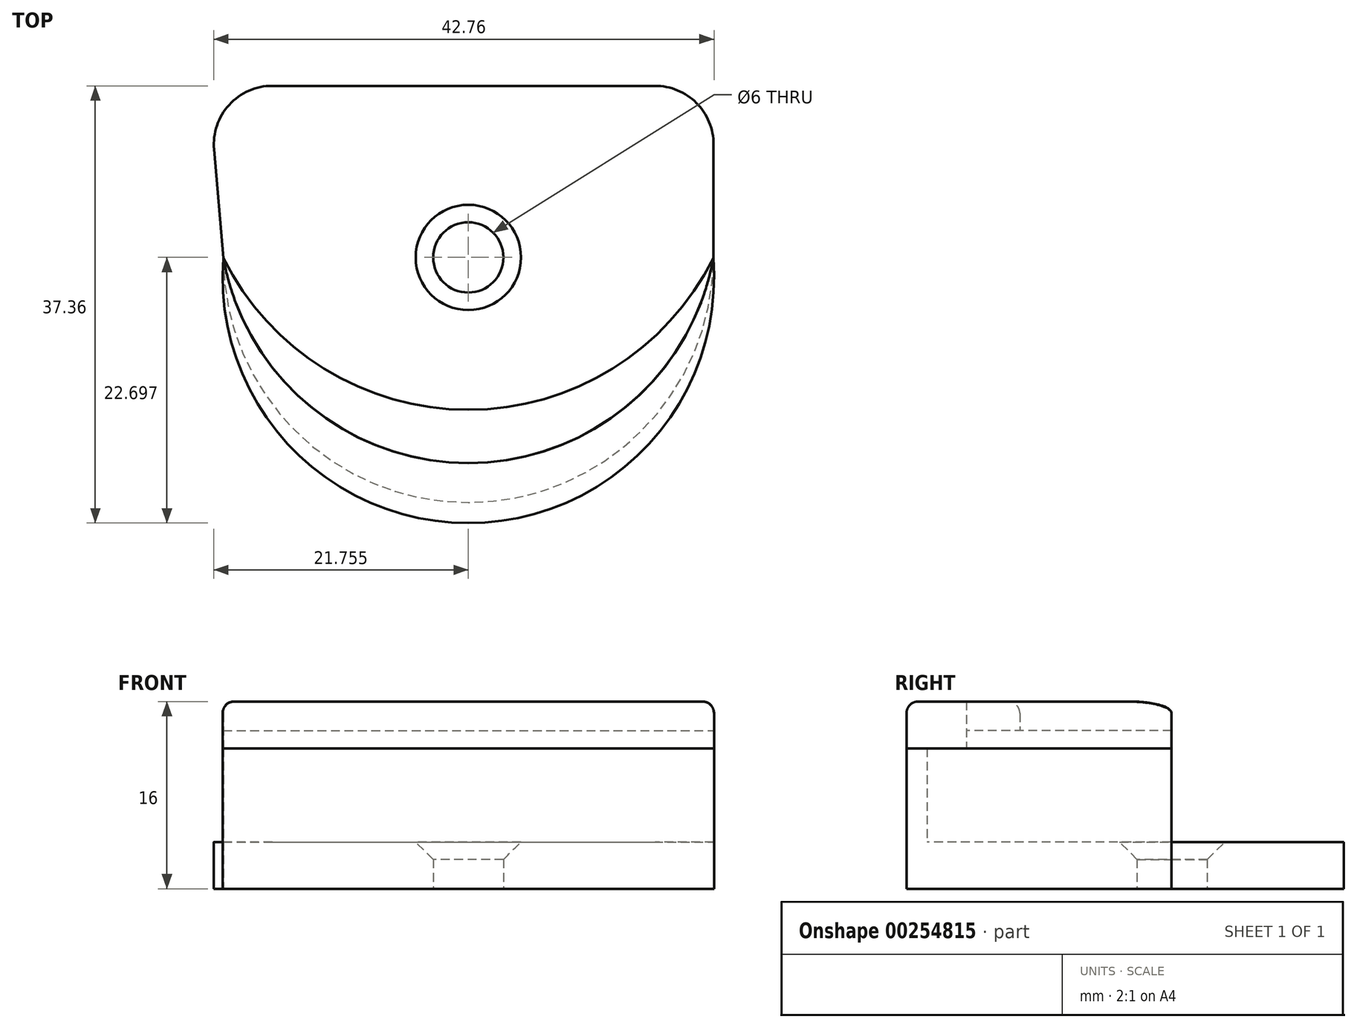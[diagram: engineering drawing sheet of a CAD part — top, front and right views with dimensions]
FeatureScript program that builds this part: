
annotation { "Feature Type Name" : "Feature", "Feature Type Description" : "" }
export const myFeature = defineFeature(function(context is Context, id is Id, definition is map)
    precondition{}
    {
        {
            var Q0;
            Q0=qCreatedBy(makeId("Top.planeOp"),FACE);
            var sketch = newSketch(context, id + "F0", { "sketchPlane" : qUnion([Q0])});
            skArc(sketch, "E0", {"start": v(-41.87, 0) * mm, "mid": v(-20.93, -22.65) * mm, "end": v(0, 0) * mm});
            skLineSegment(sketch, "E1", {"start": v(-41.87, 0) * mm, "end": v(-43.14, 14.71) * mm});
            skLineSegment(sketch, "E2", {"start": v(-43.14, 14.71) * mm, "end": v(0.03, 14.71) * mm});
            skLineSegment(sketch, "E3", {"start": v(0.03, 14.71) * mm, "end": v(0, 0) * mm});
            skArc(sketch, "E4", {"start": v(-41.87, 0) * mm, "mid": v(-20.93, -20.89) * mm, "end": v(0, 0) * mm});
            skArc(sketch, "E5", {"start": v(-41.87, 0) * mm, "mid": v(-20.93, -17.52) * mm, "end": v(0, 0) * mm});
            skCircle(sketch, "E6", {"center": v(-20.93, 0.05) * mm, "radius": 3 * mm});
            skArc(sketch, "E7", {"start": v(-41.87, 0) * mm, "mid": v(-20.93, -12.97) * mm, "end": v(0, 0) * mm});
            skSolve(sketch);
        }
        {
            var Q0;
            Q0=makeQuery(id+"F0.imprint","IMPRINT",FACE,{"disambiguationData":[TD([[makeQuery(id+"F0.imprint","IMPRINT",EDGE,{"derivedFrom":sQuery(id+"F0.wireOp",EDGE,"E1")}),-1.0]])]});
            var Q1;
            Q1=makeQuery(id+"F0.imprint","IMPRINT",FACE,{"disambiguationData":[TD([[makeQuery(id+"F0.imprint","IMPRINT",EDGE,{"derivedFrom":sQuery(id+"F0.wireOp",EDGE,"E0")}),1.0]])]});
            var Q2;
            Q2=makeQuery(id+"F0.imprint","IMPRINT",FACE,{"disambiguationData":[TD([[makeQuery(id+"F0.imprint","IMPRINT",EDGE,{"derivedFrom":sQuery(id+"F0.wireOp",EDGE,"E4")}),1.0]])]});
            var Q3;
            Q3=makeQuery(id+"F0.imprint","IMPRINT",FACE,{"disambiguationData":[TD([[makeQuery(id+"F0.imprint","IMPRINT",EDGE,{"derivedFrom":sQuery(id+"F0.wireOp",EDGE,"E5")}),1.0]])]});
            extrude(context, id + "F1", {"entities" : qUnion([Q0, Q1, Q2, Q3]), "depth" : 4 * mm});
        }
        {
            var Q0;
            Q0=makeQuery(id+"F0.imprint","IMPRINT",FACE,{"disambiguationData":[TD([[makeQuery(id+"F0.imprint","IMPRINT",EDGE,{"derivedFrom":sQuery(id+"F0.wireOp",EDGE,"E0")}),1.0]])]});
            extrude(context, id + "F2", {"entities" : qUnion([Q0]), "operationType" : NewBodyOperationType.ADD, "depth" : 12 * mm});
        }
        {
            var Q0;
            Q0=makeQuery(id+"F0.imprint","IMPRINT",FACE,{"disambiguationData":[TD([[makeQuery(id+"F0.imprint","IMPRINT",EDGE,{"derivedFrom":sQuery(id+"F0.wireOp",EDGE,"E4")}),1.0]])]});
            var Q1;
            Q1=makeQuery(id+"F0.imprint","IMPRINT",FACE,{"disambiguationData":[TD([[makeQuery(id+"F0.imprint","IMPRINT",EDGE,{"derivedFrom":sQuery(id+"F0.wireOp",EDGE,"E0")}),1.0]])]});
            extrude(context, id + "F3", {"entities" : qUnion([Q0, Q1]), "depth" : 16 * mm, "hasSecondDirection" : true, "secondDirectionOppositeDirection" : false, "secondDirectionDepth" : 12 * mm});
        }
        {
            var Q0;
            Q0=makeQuery(id+"F1.opExtrude","SWEPT_EDGE",EDGE,{"disambiguationData":[OSD([sQuery(id+"F0.wireOp",EDGE,"E2"),sQuery(id+"F0.wireOp",EDGE,"E3")])]});
            var Q1;
            Q1=makeQuery(id+"F1.opExtrude","SWEPT_EDGE",EDGE,{"disambiguationData":[OSD([sQuery(id+"F0.wireOp",EDGE,"E1"),sQuery(id+"F0.wireOp",EDGE,"E2")])]});
            fillet(context, id + "F4", {"entities" : qUnion([Q0, Q1]), "radius" : 5 * mm, "tangentPropagation" : true, "allowEdgeOverflow" : false});
        }
        {
            var Q0;
            Q0=makeQuery(id+"F0.imprint","IMPRINT",FACE,{"disambiguationData":[TD([[makeQuery(id+"F0.imprint","IMPRINT",EDGE,{"derivedFrom":sQuery(id+"F0.wireOp",EDGE,"E5")}),1.0]])]});
            extrude(context, id + "F5", {"entities" : qUnion([Q0]), "depth" : 16 * mm, "hasSecondDirection" : true, "secondDirectionOppositeDirection" : false, "secondDirectionDepth" : 13.5 * mm});
        }
        {
            var Q0;
            Q0=makeQuery(id+"F3.opExtrude","CAP_EDGE",EDGE,{"disambiguationData":[OSD([sQuery(id+"F0.wireOp",EDGE,"E0")])],"isStart":false});
            fillet(context, id + "F6", {"entities" : qUnion([Q0]), "radius" : 1 * mm, "tangentPropagation" : true, "allowEdgeOverflow" : false});
        }
        {
            var Q0;
            Q0=makeQuery(id+"F5.opExtrude","CAP_EDGE",EDGE,{"disambiguationData":[OSD([sQuery(id+"F0.wireOp",EDGE,"E7")])],"isStart":false});
            fillet(context, id + "F7", {"entities" : qUnion([Q0]), "radius" : 1 * mm, "tangentPropagation" : true, "allowEdgeOverflow" : false});
        }
        {
            var Q0;
            Q0=makeQuery(id+"F1.opExtrude","CAP_EDGE",EDGE,{"disambiguationData":[OSD([sQuery(id+"F0.wireOp",EDGE,"E6")])],"isStart":false});
            chamfer(context, id + "F8", {"entities" : qUnion([Q0]), "width" : 1.5 * mm, "tangentPropagation" : true});
        }
    });
